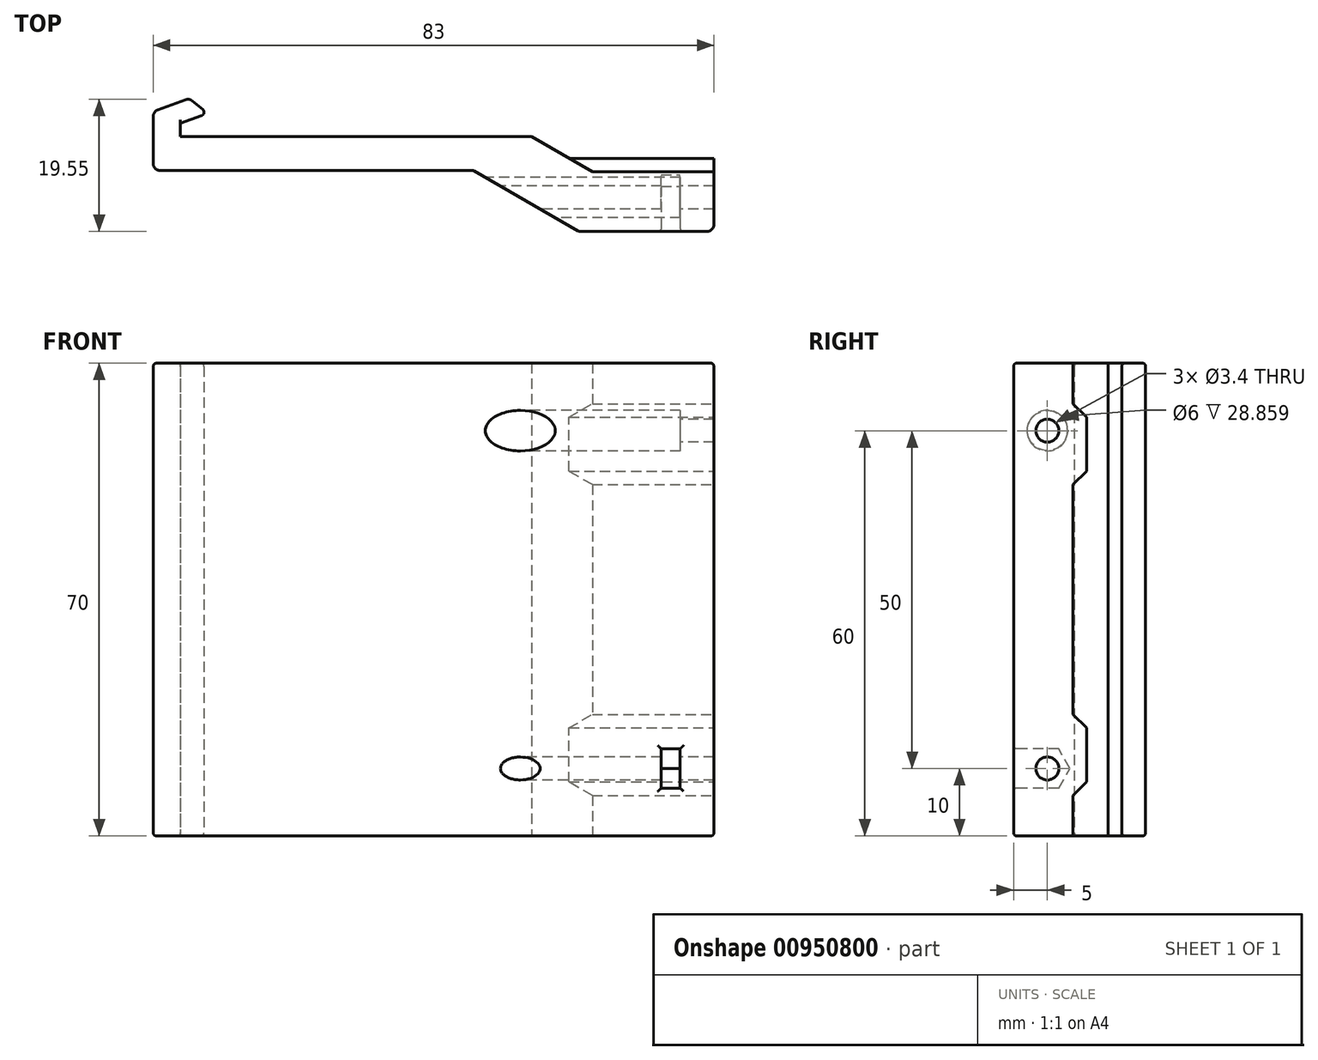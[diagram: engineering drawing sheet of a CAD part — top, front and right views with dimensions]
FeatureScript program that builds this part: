
annotation { "Feature Type Name" : "Feature", "Feature Type Description" : "" }
export const myFeature = defineFeature(function(context is Context, id is Id, definition is map)
    precondition{}
    {
        {
            var Q0;
            Q0=qCreatedBy(makeId("Top.planeOp"),FACE);
            var sketch = newSketch(context, id + "F0", { "sketchPlane" : qUnion([Q0])});
            skLineSegment(sketch, "E0", {"start": v(-27, 0) * mm, "end": v(-79, 0) * mm});
            skLineSegment(sketch, "E1", {"start": v(-79, 0) * mm, "end": v(-79, 2) * mm});
            skLineSegment(sketch, "E2", {"start": v(-79, 2) * mm, "end": v(-75.81, 3.16) * mm});
            skLineSegment(sketch, "E3", {"start": v(-75.66, 4.01) * mm, "end": v(-77.21, 5.31) * mm});
            skLineSegment(sketch, "E4", {"start": v(-78.2, 5.49) * mm, "end": v(-82.34, 3.98) * mm});
            skLineSegment(sketch, "E5", {"start": v(-83, 3.04) * mm, "end": v(-83, -4) * mm});
            skLineSegment(sketch, "E6", {"start": v(-82, -5) * mm, "end": v(-35.59, -5) * mm});
            skLineSegment(sketch, "E7", {"start": v(0, -5.2) * mm, "end": v(0, -13) * mm});
            skLineSegment(sketch, "E8", {"start": v(-1, -14) * mm, "end": v(-20, -14) * mm});
            skLineSegment(sketch, "E9", {"start": v(-20, -14) * mm, "end": v(-35.59, -5) * mm});
            skPoint(sketch, "E10.visualSharp", {"position": v(-77.65, 5.68) * mm});
            skArc(sketch, "E10.filletArc", {"start": v(-77.21, 5.31) * mm, "mid": v(-77.68, 5.53) * mm, "end": v(-78.2, 5.49) * mm});
            skPoint(sketch, "E11.visualSharp", {"position": v(-83, 3.74) * mm});
            skArc(sketch, "E11.filletArc", {"start": v(-82.34, 3.98) * mm, "mid": v(-82.82, 3.61) * mm, "end": v(-83, 3.04) * mm});
            skPoint(sketch, "E12.visualSharp", {"position": v(-83, -5) * mm});
            skArc(sketch, "E12.filletArc", {"start": v(-83, -4) * mm, "mid": v(-82.7, -4.7) * mm, "end": v(-82, -5) * mm});
            skPoint(sketch, "E13.visualSharp", {"position": v(0, -14) * mm});
            skArc(sketch, "E13.filletArc", {"start": v(-1, -14) * mm, "mid": v(-0.3, -13.7) * mm, "end": v(0, -13) * mm});
            skPoint(sketch, "E14.visualSharp", {"position": v(-20, -14) * mm});
            skPoint(sketch, "E15.visualSharp", {"position": v(-35.59, -5) * mm});
            skPoint(sketch, "E16.visualSharp", {"position": v(-75, 3.46) * mm});
            skArc(sketch, "E16.filletArc", {"start": v(-75.81, 3.16) * mm, "mid": v(-75.5, 3.54) * mm, "end": v(-75.66, 4.01) * mm});
            skLineSegment(sketch, "E17", {"start": v(0, -5.2) * mm, "end": v(-18, -5.2) * mm});
            skLineSegment(sketch, "E18", {"start": v(-18, -5.2) * mm, "end": v(-27, 0) * mm});
            skPoint(sketch, "E19.orphan", {"position": v(0, 0) * mm});
            skSolve(sketch);
        }
        {
            var Q0;
            Q0=makeQuery(id+"F0.imprint","IMPRINT",FACE,{"disambiguationData":[TD([[makeQuery(id+"F0.imprint","IMPRINT",EDGE,{"derivedFrom":sQuery(id+"F0.wireOp",EDGE,"E0")}),1.0]])]});
            extrude(context, id + "F1", {"entities" : qUnion([Q0]), "depth" : 70 * mm, "offsetDistance" : 25 * mm});
        }
        {
            var Q0;
            Q0=makeQuery(id+"F1.opExtrude","SWEPT_FACE",FACE,{"disambiguationData":[OSD([sQuery(id+"F0.wireOp",EDGE,"E5")])]});
            var sketch = newSketch(context, id + "F2", { "sketchPlane" : qUnion([Q0])});
            skPoint(sketch, "E20", {"position": v(9, 60) * mm});
            skPoint(sketch, "E21", {"position": v(9, 10) * mm});
            skLineSegment(sketch, "E22", {"start": v(9, 10) * mm, "end": v(9, 60) * mm, "construction": true});
            skPoint(sketch, "E23", {"position": v(4, 35) * mm});
            skPoint(sketch, "E24", {"position": v(9, 35) * mm});
            skLineSegment(sketch, "E25", {"start": v(9, 35) * mm, "end": v(4, 35) * mm, "construction": true});
            skCircle(sketch, "E26.cCircle", {"center": v(9, 10) * mm, "radius": 2.9 * mm, "construction": true});
            skLineSegment(sketch, "E26.0", {"start": v(12.35, 10) * mm, "end": v(10.67, 7.1) * mm});
            skLineSegment(sketch, "E26.1", {"start": v(10.67, 7.1) * mm, "end": v(7.33, 7.1) * mm});
            skLineSegment(sketch, "E26.2", {"start": v(7.33, 7.1) * mm, "end": v(5.65, 10) * mm});
            skLineSegment(sketch, "E26.3", {"start": v(5.65, 10) * mm, "end": v(7.33, 12.9) * mm});
            skLineSegment(sketch, "E26.4", {"start": v(7.33, 12.9) * mm, "end": v(10.67, 12.9) * mm});
            skLineSegment(sketch, "E26.5", {"start": v(10.67, 12.9) * mm, "end": v(12.35, 10) * mm});
            skPoint(sketch, "E26.0.midPoint", {"position": v(11.51, 8.55) * mm});
            skSolve(sketch);
        }
        {
            var Q0;
            Q0=sQuery(id+"F2.wireOp",VERTEX,"E21");
            var Q1;
            Q1=makeQuery(id+"F1.opExtrude","SWEPT_BODY",BODY,{"disambiguationData":[OSD([sQuery(id+"F0.wireOp",EDGE,"E0"),sQuery(id+"F0.wireOp",EDGE,"E1"),sQuery(id+"F0.wireOp",EDGE,"E2"),sQuery(id+"F0.wireOp",EDGE,"E3"),sQuery(id+"F0.wireOp",EDGE,"E4"),sQuery(id+"F0.wireOp",EDGE,"E5"),sQuery(id+"F0.wireOp",EDGE,"E6"),sQuery(id+"F0.wireOp",EDGE,"E7"),sQuery(id+"F0.wireOp",EDGE,"E8"),sQuery(id+"F0.wireOp",EDGE,"E9"),sQuery(id+"F0.wireOp",EDGE,"E10.filletArc"),sQuery(id+"F0.wireOp",EDGE,"E11.filletArc"),sQuery(id+"F0.wireOp",EDGE,"E12.filletArc"),sQuery(id+"F0.wireOp",EDGE,"E13.filletArc"),sQuery(id+"F0.wireOp",EDGE,"E14.filletArc"),sQuery(id+"F0.wireOp",EDGE,"E15.filletArc"),sQuery(id+"F0.wireOp",EDGE,"E16.filletArc"),sQuery(id+"F0.wireOp",EDGE,"E17"),sQuery(id+"F0.wireOp",EDGE,"E18")])]});
            hole(context, id + "F3", {"style" : HoleStyle.C_SINK, "endStyle" : HoleEndStyle.BLIND, "holeDiameter" : 3.4 * mm, "cSinkDiameter" : 4 * mm, "cSinkAngle" : 90 * degree, "majorDiameter" : 5 * mm, "holeDepth" : 90 * mm, "isTappedThrough" : true, "tappedDepth" : 12 * mm, "tapClearance" : 3, "startFromSketch" : true, "locations" : qUnion([Q0]), "scope" : qUnion([Q1])});
        }
        {
            var Q0;
            Q0=sQuery(id+"F2.wireOp",VERTEX,"E20");
            var Q1;
            Q1=makeQuery(id+"F1.opExtrude","SWEPT_BODY",BODY,{"disambiguationData":[OSD([sQuery(id+"F0.wireOp",EDGE,"E0"),sQuery(id+"F0.wireOp",EDGE,"E1"),sQuery(id+"F0.wireOp",EDGE,"E2"),sQuery(id+"F0.wireOp",EDGE,"E3"),sQuery(id+"F0.wireOp",EDGE,"E4"),sQuery(id+"F0.wireOp",EDGE,"E5"),sQuery(id+"F0.wireOp",EDGE,"E6"),sQuery(id+"F0.wireOp",EDGE,"E7"),sQuery(id+"F0.wireOp",EDGE,"E8"),sQuery(id+"F0.wireOp",EDGE,"E9"),sQuery(id+"F0.wireOp",EDGE,"E10.filletArc"),sQuery(id+"F0.wireOp",EDGE,"E11.filletArc"),sQuery(id+"F0.wireOp",EDGE,"E12.filletArc"),sQuery(id+"F0.wireOp",EDGE,"E13.filletArc"),sQuery(id+"F0.wireOp",EDGE,"E14.filletArc"),sQuery(id+"F0.wireOp",EDGE,"E15.filletArc"),sQuery(id+"F0.wireOp",EDGE,"E16.filletArc"),sQuery(id+"F0.wireOp",EDGE,"E17"),sQuery(id+"F0.wireOp",EDGE,"E18")])]});
            hole(context, id + "F4", {"style" : HoleStyle.C_BORE, "endStyle" : HoleEndStyle.THROUGH, "holeDiameter" : 3.4 * mm, "cBoreDiameter" : 6 * mm, "cBoreDepth" : 78 * mm, "majorDiameter" : 5 * mm, "isTappedThrough" : true, "tappedDepth" : 12 * mm, "tapClearance" : 3, "startFromSketch" : true, "locations" : qUnion([Q0]), "scope" : qUnion([Q1])});
        }
        {
            var Q0;
            Q0=makeQuery(id+"F1.opExtrude","SWEPT_FACE",FACE,{"disambiguationData":[OSD([sQuery(id+"F0.wireOp",EDGE,"E7")])]});
            var sketch = newSketch(context, id + "F5", { "sketchPlane" : qUnion([Q0])});
            skLineSegment(sketch, "E27", {"start": v(-5.2, 52) * mm, "end": v(-3.2, 54) * mm});
            skLineSegment(sketch, "E28", {"start": v(-3.2, 54) * mm, "end": v(-3.2, 62) * mm});
            skLineSegment(sketch, "E29", {"start": v(-3.2, 62) * mm, "end": v(-5.2, 64) * mm});
            skLineSegment(sketch, "E30", {"start": v(-5.2, 64) * mm, "end": v(-5.2, 52) * mm});
            skLineSegment(sketch, "E31.MirrorCS", {"start": v(4.8, 62) * mm, "end": v(-3.2, 62) * mm});
            skLineSegment(sketch, "E32.1.0.0", {"start": v(-3.2, 16) * mm, "end": v(-5.2, 18) * mm});
            skLineSegment(sketch, "E32.1.0.1", {"start": v(-3.2, 8) * mm, "end": v(-3.2, 16) * mm});
            skLineSegment(sketch, "E32.1.0.2", {"start": v(-5.2, 6) * mm, "end": v(-3.2, 8) * mm});
            skLineSegment(sketch, "E32.1.0.3", {"start": v(-5.2, 18) * mm, "end": v(-5.2, 6) * mm});
            skLineSegment(sketch, "E32.direction1", {"start": v(-5.2, 52) * mm, "end": v(-5.2, 6) * mm, "construction": true});
            skSolve(sketch);
        }
        {
            var Q0;
            Q0=makeQuery(id+"F5.imprint","IMPRINT",FACE,{"disambiguationData":[TD([[makeQuery(id+"F5.imprint","IMPRINT",EDGE,{"derivedFrom":sQuery(id+"F5.wireOp",EDGE,"E27")}),1.0]])]});
            var Q1;
            Q1=makeQuery(id+"F5.imprint","IMPRINT",FACE,{"disambiguationData":[TD([[makeQuery(id+"F5.imprint","IMPRINT",EDGE,{"derivedFrom":sQuery(id+"F5.wireOp",EDGE,"E32.1.0.0")}),1.0]])]});
            var Q2;
            Q2=makeQuery(id+"F1.opExtrude","SWEPT_FACE",FACE,{"disambiguationData":[OSD([sQuery(id+"F0.wireOp",EDGE,"E18")])]});
            extrude(context, id + "F6", {"entities" : qUnion([Q0, Q1]), "operationType" : NewBodyOperationType.ADD, "endBound" : BoundingType.UP_TO_SURFACE, "oppositeDirection" : true, "depth" : 25 * mm, "endBoundEntityFace" : qUnion([Q2]), "offsetDistance" : 25 * mm});
        }
        {
            var Q0;
            Q0=qCreatedBy(makeId("Right.planeOp"),FACE);
            cPlane(context, id + "F7", {"entities" : qUnion([Q0]), "cplaneType" : CPlaneType.OFFSET, "offset" : 5 * mm, "oppositeDirection" : true, "width" : 150 * mm, "height" : 150 * mm});
        }
        {
            var Q0;
            Q0=qCreatedBy(id+"F7.planeOp",FACE);
            var sketch = newSketch(context, id + "F8", { "sketchPlane" : qUnion([Q0])});
            skLineSegment(sketch, "E33.0", {"start": v(-10.67, 7.1) * mm, "end": v(-7.33, 7.1) * mm});
            skLineSegment(sketch, "E34.0", {"start": v(-7.33, 12.9) * mm, "end": v(-10.67, 12.9) * mm});
            skLineSegment(sketch, "E35.0", {"start": v(-5.65, 10) * mm, "end": v(-7.33, 12.9) * mm});
            skLineSegment(sketch, "E36.0", {"start": v(-7.33, 7.1) * mm, "end": v(-5.65, 10) * mm});
            skLineSegment(sketch, "E37", {"start": v(-10.67, 7.1) * mm, "end": v(-14, 7.1) * mm});
            skLineSegment(sketch, "E38", {"start": v(-14, 7.1) * mm, "end": v(-14, 12.9) * mm});
            skLineSegment(sketch, "E39", {"start": v(-14, 12.9) * mm, "end": v(-10.67, 12.9) * mm});
            skSolve(sketch);
        }
        {
            var Q0;
            Q0 = qSketchRegion(id + "F8", true);
            extrude(context, id + "F9", {"entities" : qUnion([Q0]), "operationType" : NewBodyOperationType.REMOVE, "oppositeDirection" : true, "depth" : 2.8 * mm, "offsetDistance" : 25 * mm});
        }
        {
            var Q0;
            Q0=makeQuery(id+"F4.hole-0.boolean.opBoolean","INTERSECT",EDGE,{"derivedFrom":[makeQuery(id+"F1.opExtrude","SWEPT_FACE",FACE,{"disambiguationData":[OSD([sQuery(id+"F0.wireOp",EDGE,"E9")])]}),makeQuery(id+"F4.hole-0.opRevolve","SWEPT_FACE",FACE,{"disambiguationData":[OSD([sQuery(id+"F4.hole-0.sketch.wireOp",EDGE,"cbore_start_line_2")])]})]});
            var Q1;
            Q1=makeQuery(id+"F4.hole-0.boolean.opBoolean","INTERSECT",EDGE,{"derivedFrom":[makeQuery(id+"F1.opExtrude","SWEPT_FACE",FACE,{"disambiguationData":[OSD([sQuery(id+"F0.wireOp",EDGE,"E7")])]}),makeQuery(id+"F4.hole-0.opRevolve","SWEPT_FACE",FACE,{"disambiguationData":[OSD([sQuery(id+"F4.hole-0.sketch.wireOp",EDGE,"core_line_2")])]})]});
            var Q2;
            Q2=makeQuery(id+"F3.hole-0.boolean.opBoolean","INTERSECT",EDGE,{"derivedFrom":[makeQuery(id+"F1.opExtrude","SWEPT_FACE",FACE,{"disambiguationData":[OSD([sQuery(id+"F0.wireOp",EDGE,"E7")])]}),makeQuery(id+"F3.hole-0.opRevolve","SWEPT_FACE",FACE,{"disambiguationData":[OSD([sQuery(id+"F3.hole-0.sketch.wireOp",EDGE,"core_line_2")])]})]});
            var Q3;
            Q3=makeQuery(id+"F3.hole-0.boolean.opBoolean","INTERSECT",EDGE,{"derivedFrom":[makeQuery(id+"F1.opExtrude","SWEPT_FACE",FACE,{"disambiguationData":[OSD([sQuery(id+"F0.wireOp",EDGE,"E9")])]}),makeQuery(id+"F3.hole-0.opRevolve","SWEPT_FACE",FACE,{"disambiguationData":[OSD([sQuery(id+"F3.hole-0.sketch.wireOp",EDGE,"core_line_2")])]})]});
            var Q4;
            Q4=makeQuery(id+"F1.opExtrude","SWEPT_FACE",FACE,{"disambiguationData":[OSD([sQuery(id+"F0.wireOp",EDGE,"E8")])]});
            var Q5;
            Q5=makeQuery(id+"F1.opExtrude","SWEPT_EDGE",EDGE,{"disambiguationData":[OSD([sQuery(id+"F0.wireOp",EDGE,"E6"),sQuery(id+"F0.wireOp",EDGE,"E9")])]});
            var Q6;
            Q6=makeQuery(id+"F1.opExtrude","CAP_EDGE",EDGE,{"disambiguationData":[OSD([sQuery(id+"F0.wireOp",EDGE,"E9")])],"isStart":false});
            var Q7;
            Q7=makeQuery(id+"F1.opExtrude","CAP_EDGE",EDGE,{"disambiguationData":[OSD([sQuery(id+"F0.wireOp",EDGE,"E6")])],"isStart":false});
            var Q8;
            Q8=makeQuery(id+"F1.opExtrude","CAP_EDGE",EDGE,{"disambiguationData":[OSD([sQuery(id+"F0.wireOp",EDGE,"E6")])],"isStart":true});
            var Q9;
            Q9=makeQuery(id+"F1.opExtrude","CAP_EDGE",EDGE,{"disambiguationData":[OSD([sQuery(id+"F0.wireOp",EDGE,"E9")])],"isStart":true});
            fillet(context, id + "F10", {"entities" : qUnion([Q0, Q1, Q2, Q3, Q4, Q5, Q6, Q7, Q8, Q9]), "radius" : .5 * mm, "tangentPropagation" : true, "allowEdgeOverflow" : false});
        }
    });
